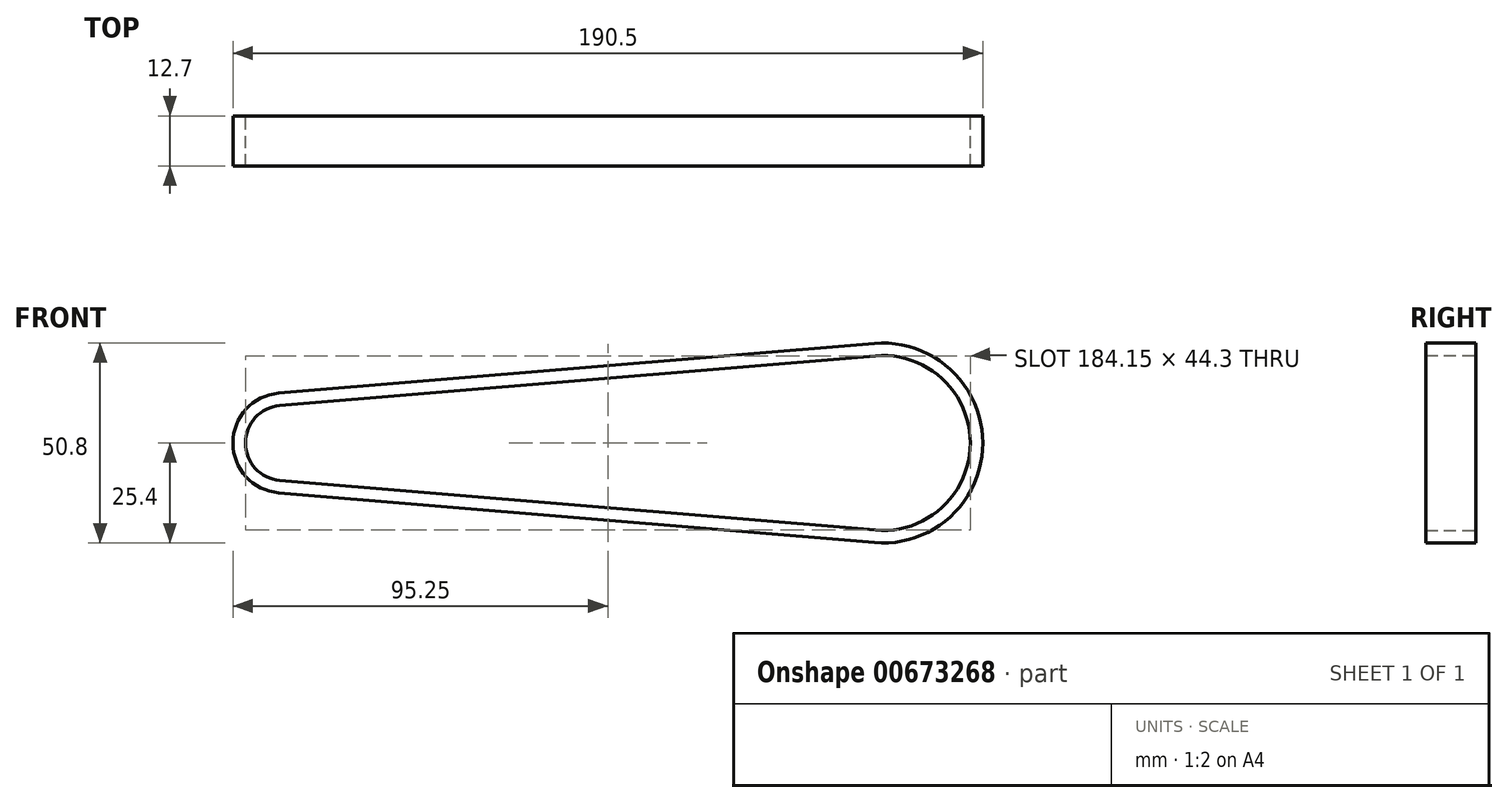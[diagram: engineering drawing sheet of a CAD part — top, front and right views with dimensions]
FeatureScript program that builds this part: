
annotation { "Feature Type Name" : "Feature", "Feature Type Description" : "" }
export const myFeature = defineFeature(function(context is Context, id is Id, definition is map)
    precondition{}
    {
        {
            var Q0;
            Q0=qCreatedBy(makeId("Front.planeOp"),FACE);
            var sketch = newSketch(context, id + "F0", { "sketchPlane" : qUnion([Q0])});
            skArc(sketch, "E0", {"start": v(-0.8, 9.5) * mm, "mid": v(-9.53, 0) * mm, "end": v(-0.8, -9.5) * mm});
            skArc(sketch, "E1", {"start": v(-1.06, 12.66) * mm, "mid": v(-12.7, 0) * mm, "end": v(-1.06, -12.66) * mm});
            skArc(sketch, "E2", {"start": v(150.55, -22.15) * mm, "mid": v(174.62, 0) * mm, "end": v(150.55, 22.15) * mm});
            skArc(sketch, "E3", {"start": v(150.28, -25.31) * mm, "mid": v(177.8, 0) * mm, "end": v(150.28, 25.31) * mm});
            skLineSegment(sketch, "E4", {"start": v(-1.06, 12.66) * mm, "end": v(150.28, 25.31) * mm});
            skLineSegment(sketch, "E5", {"start": v(-1.06, -12.66) * mm, "end": v(150.28, -25.31) * mm});
            skLineSegment(sketch, "E6", {"start": v(-0.8, 9.5) * mm, "end": v(150.55, 22.15) * mm});
            skLineSegment(sketch, "E7", {"start": v(-0.8, -9.5) * mm, "end": v(150.55, -22.15) * mm});
            skSolve(sketch);
        }
        {
            var Q0;
            Q0=qSketchRegion(id+"F0",true);
            extrude(context, id + "F1", {"entities" : qUnion([Q0]), "depth" : 12.7 * mm});
        }
    });
